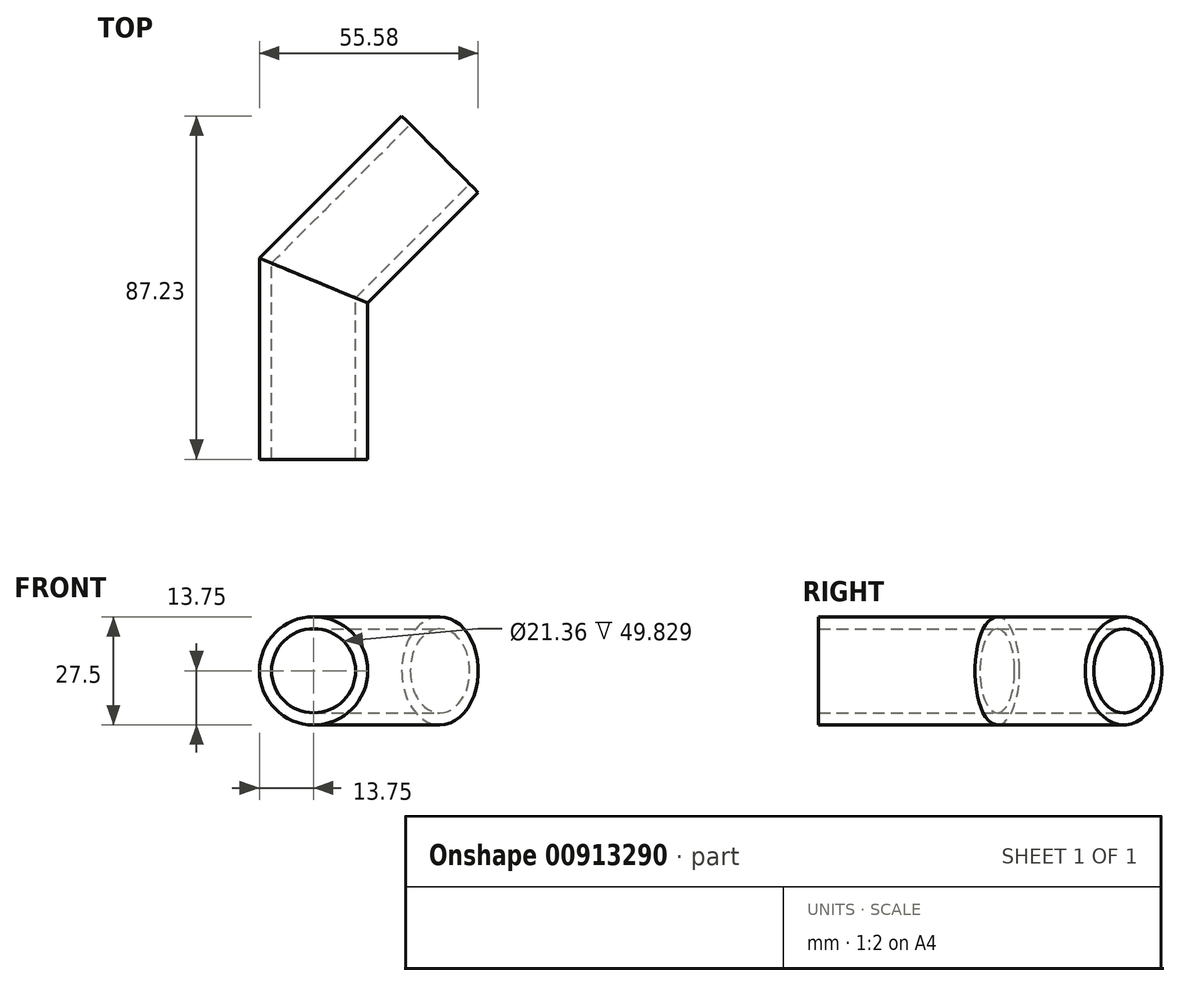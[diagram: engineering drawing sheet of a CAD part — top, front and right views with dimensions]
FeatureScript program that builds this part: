
annotation { "Feature Type Name" : "Feature", "Feature Type Description" : "" }
export const myFeature = defineFeature(function(context is Context, id is Id, definition is map)
    precondition{}
    {
        {
            var Q0;
            Q0=qCreatedBy(makeId("Front.planeOp"),FACE);
            cPlane(context, id + "F0", {"entities" : qUnion([Q0]), "cplaneType" : CPlaneType.OFFSET, "offset" : 31.65 * mm, "width" : 152.4 * mm, "height" : 152.4 * mm});
        }
        {
            var Q0;
            Q0=qCreatedBy(id+"F0.planeOp",FACE);
            var sketch = newSketch(context, id + "F1", { "sketchPlane" : qUnion([Q0])});
            skCircle(sketch, "E0", {"center": v(0, 0) * mm, "radius": 13.75 * mm});
            skCircle(sketch, "E1", {"center": v(0, 0) * mm, "radius": 10.68 * mm});
            skSolve(sketch);
        }
        {
            var Q0;
            Q0=qCreatedBy(makeId("Top.planeOp"),FACE);
            var sketch = newSketch(context, id + "F2", { "sketchPlane" : qUnion([Q0])});
            skPoint(sketch, "E2.0", {"position": v(0, -31.65) * mm});
            skLineSegment(sketch, "E3", {"start": v(0, -31.65) * mm, "end": v(0, 13.75) * mm});
            skLineSegment(sketch, "E4", {"start": v(0, 13.75) * mm, "end": v(32.1, 45.86) * mm});
            skPoint(sketch, "E5.visualSharp", {"position": v(0, 13.75) * mm});
            skSolve(sketch);
        }
        {
            var Q0;
            Q0=makeQuery(id+"F1.imprint","IMPRINT",FACE,{"disambiguationData":[TD([[makeQuery(id+"F1.imprint","IMPRINT",EDGE,{"derivedFrom":sQuery(id+"F1.wireOp",EDGE,"E0")}),1.0]])]});
            var Q1;
            Q1=sQuery(id+"F2.wireOp",EDGE,"E5.filletArc");
            var Q2;
            Q2=sQuery(id+"F2.wireOp",EDGE,"E3");
            var Q3;
            Q3=sQuery(id+"F2.wireOp",EDGE,"E4");
            sweep(context, id + "F3", {"profiles" : qUnion([Q0]), "path" : qUnion([Q1, Q2, Q3])});
        }
    });
